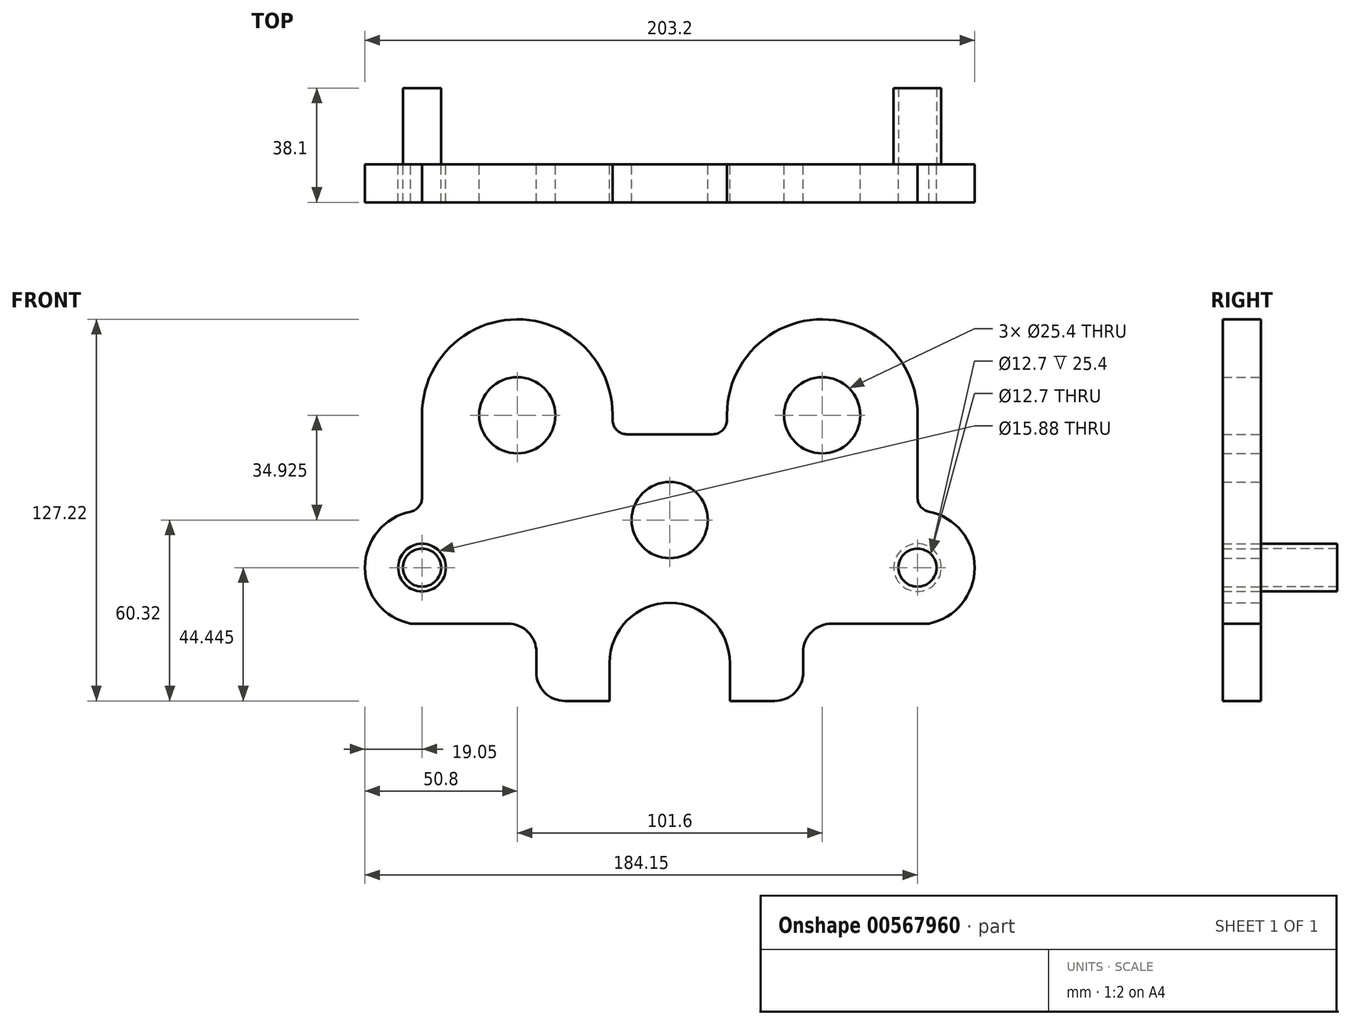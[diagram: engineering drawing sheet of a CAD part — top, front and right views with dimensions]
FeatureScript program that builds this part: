
annotation { "Feature Type Name" : "Feature", "Feature Type Description" : "" }
export const myFeature = defineFeature(function(context is Context, id is Id, definition is map)
    precondition{}
    {
        {
            var Q0;
            Q0=qCreatedBy(makeId("Front.planeOp"),FACE);
            var sketch = newSketch(context, id + "F0", { "sketchPlane" : qUnion([Q0])});
            skLineSegment(sketch, "E0", {"start": v(0, 79.1) * mm, "end": v(0, -74.39) * mm, "construction": true});
            skLineSegment(sketch, "E1", {"start": v(-86.36, 0) * mm, "end": v(95.43, 0) * mm, "construction": true});
            skLineSegment(sketch, "E2", {"start": v(50.8, 47.26) * mm, "end": v(50.8, 24.4) * mm, "construction": true});
            skLineSegment(sketch, "E3", {"start": v(82.55, -4.26) * mm, "end": v(82.55, -30.93) * mm, "construction": true});
            skLineSegment(sketch, "E4", {"start": v(-25.4, -47.62) * mm, "end": v(22.13, -47.62) * mm, "construction": true});
            skLineSegment(sketch, "E5", {"start": v(63.27, -15.88) * mm, "end": v(102.7, -15.88) * mm, "construction": true});
            skLineSegment(sketch, "E6", {"start": v(31.78, 34.93) * mm, "end": v(71.21, 34.93) * mm, "construction": true});
            skPoint(sketch, "E7", {"position": v(50.8, 34.93) * mm});
            skPoint(sketch, "E8", {"position": v(82.55, -15.88) * mm});
            skPoint(sketch, "E9", {"position": v(0, -47.62) * mm});
            skCircle(sketch, "E10", {"center": v(50.8, 34.93) * mm, "radius": 12.7 * mm});
            skCircle(sketch, "E11", {"center": v(82.55, -15.88) * mm, "radius": 6.35 * mm});
            skCircle(sketch, "E12", {"center": v(0, 0) * mm, "radius": 12.7 * mm});
            skLineSegment(sketch, "E13", {"start": v(-14.29, 28.57) * mm, "end": v(14.29, 28.57) * mm});
            skLineSegment(sketch, "E14", {"start": v(19.05, 35.15) * mm, "end": v(19.05, 33.34) * mm});
            skLineSegment(sketch, "E15", {"start": v(82.55, 34.93) * mm, "end": v(82.55, 7.46) * mm});
            skLineSegment(sketch, "E16", {"start": v(20.02, -60.32) * mm, "end": v(34.93, -60.32) * mm});
            skLineSegment(sketch, "E17", {"start": v(44.45, -50.8) * mm, "end": v(44.45, -44.07) * mm});
            skLineSegment(sketch, "E18", {"start": v(53.98, -34.54) * mm, "end": v(82.55, -34.54) * mm});
            skLineSegment(sketch, "E19", {"start": v(82.55, -34.54) * mm, "end": v(86.36, -34.54) * mm});
            skArc(sketch, "E20", {"start": v(19.05, 35.15) * mm, "mid": v(50.91, 66.9) * mm, "end": v(82.55, 34.93) * mm});
            skPoint(sketch, "E21.visualSharp", {"position": v(44.45, -34.54) * mm});
            skArc(sketch, "E21.filletArc", {"start": v(53.98, -34.54) * mm, "mid": v(47.24, -37.33) * mm, "end": v(44.45, -44.07) * mm});
            skPoint(sketch, "E22.visualSharp", {"position": v(44.45, -60.32) * mm});
            skArc(sketch, "E22.filletArc", {"start": v(34.93, -60.32) * mm, "mid": v(41.66, -57.54) * mm, "end": v(44.45, -50.8) * mm});
            skPoint(sketch, "E23.visualSharp", {"position": v(82.55, 3.18) * mm});
            skArc(sketch, "E23.filletArc", {"start": v(82.55, 7.46) * mm, "mid": v(83.62, 4.44) * mm, "end": v(86.36, 2.8) * mm});
            skArc(sketch, "E24", {"start": v(86.36, 2.8) * mm, "mid": v(101.6, -15.88) * mm, "end": v(86.36, -34.54) * mm});
            skLineSegment(sketch, "E25", {"start": v(20.02, -60.33) * mm, "end": v(20.02, -47.62) * mm});
            skLineSegment(sketch, "E26.MirrorCS", {"start": v(-20.02, -60.33) * mm, "end": v(-20.02, -47.62) * mm});
            skLineSegment(sketch, "E27.MirrorCS", {"start": v(-20.02, -60.32) * mm, "end": v(-34.93, -60.32) * mm});
            skArc(sketch, "E28.MirrorCS", {"start": v(-34.93, -60.32) * mm, "mid": v(-41.66, -57.54) * mm, "end": v(-44.45, -50.8) * mm});
            skLineSegment(sketch, "E29.MirrorCS", {"start": v(-44.45, -50.8) * mm, "end": v(-44.45, -44.07) * mm});
            skArc(sketch, "E30.MirrorCS", {"start": v(-53.98, -34.54) * mm, "mid": v(-47.24, -37.33) * mm, "end": v(-44.45, -44.07) * mm});
            skLineSegment(sketch, "E31.MirrorCS", {"start": v(-53.98, -34.54) * mm, "end": v(-82.55, -34.54) * mm});
            skLineSegment(sketch, "E32.MirrorCS", {"start": v(-82.55, -34.54) * mm, "end": v(-86.36, -34.54) * mm});
            skArc(sketch, "E33.MirrorCS", {"start": v(-86.36, 2.8) * mm, "mid": v(-101.6, -15.88) * mm, "end": v(-86.36, -34.54) * mm});
            skArc(sketch, "E34.MirrorCS", {"start": v(-82.55, 7.46) * mm, "mid": v(-83.62, 4.44) * mm, "end": v(-86.36, 2.8) * mm});
            skLineSegment(sketch, "E35.MirrorCS", {"start": v(-82.55, 34.93) * mm, "end": v(-82.55, 7.46) * mm});
            skArc(sketch, "E36.MirrorCS", {"start": v(-19.05, 35.15) * mm, "mid": v(-50.91, 66.9) * mm, "end": v(-82.55, 34.93) * mm});
            skLineSegment(sketch, "E37.MirrorCS", {"start": v(-19.05, 35.15) * mm, "end": v(-19.05, 33.34) * mm});
            skArc(sketch, "E38", {"start": v(-20.02, -47.62) * mm, "mid": v(0, -27.6) * mm, "end": v(20.02, -47.62) * mm});
            skCircle(sketch, "E39.MirrorC", {"center": v(-50.8, 34.93) * mm, "radius": 12.7 * mm});
            skCircle(sketch, "E40.MirrorC", {"center": v(-82.55, -15.88) * mm, "radius": 6.35 * mm});
            skPoint(sketch, "E41.visualSharp", {"position": v(-19.05, 28.57) * mm});
            skArc(sketch, "E41.filletArc", {"start": v(-19.05, 33.34) * mm, "mid": v(-17.66, 29.97) * mm, "end": v(-14.29, 28.57) * mm});
            skPoint(sketch, "E42.visualSharp", {"position": v(19.05, 28.58) * mm});
            skArc(sketch, "E42.filletArc", {"start": v(14.29, 28.57) * mm, "mid": v(17.66, 29.97) * mm, "end": v(19.05, 33.34) * mm});
            skCircle(sketch, "E43", {"center": v(82.55, -15.88) * mm, "radius": 7.94 * mm});
            skCircle(sketch, "E44.MirrorC", {"center": v(-82.55, -15.88) * mm, "radius": 7.94 * mm});
            skSolve(sketch);
        }
        {
            var Q0;
            Q0=makeQuery(id+"F0.imprint","IMPRINT",FACE,{"disambiguationData":[TD([[makeQuery(id+"F0.imprint","IMPRINT",EDGE,{"derivedFrom":sQuery(id+"F0.wireOp",EDGE,"E10")}),-1.0]])]});
            var Q1;
            Q1=makeQuery(id+"F0.imprint","IMPRINT",FACE,{"disambiguationData":[TD([[makeQuery(id+"F0.imprint","IMPRINT",EDGE,{"derivedFrom":sQuery(id+"F0.wireOp",EDGE,"E11")}),-1.0]])]});
            var Q2;
            Q2=makeQuery(id+"F0.imprint","IMPRINT",FACE,{"disambiguationData":[TD([[makeQuery(id+"F0.imprint","IMPRINT",EDGE,{"derivedFrom":sQuery(id+"F0.wireOp",EDGE,"E40.MirrorC")}),1.0]])]});
            extrude(context, id + "F1", {"entities" : qUnion([Q0, Q1, Q2]), "depth" : 12.7 * mm, "offsetDistance" : 25.4 * mm});
        }
        {
            var Q0;
            Q0=makeQuery(id+"F0.imprint","IMPRINT",FACE,{"disambiguationData":[TD([[makeQuery(id+"F0.imprint","IMPRINT",EDGE,{"derivedFrom":sQuery(id+"F0.wireOp",EDGE,"E40.MirrorC")}),1.0]])]});
            var Q1;
            Q1=makeQuery(id+"F0.imprint","IMPRINT",FACE,{"disambiguationData":[TD([[makeQuery(id+"F0.imprint","IMPRINT",EDGE,{"derivedFrom":sQuery(id+"F0.wireOp",EDGE,"E11")}),-1.0]])]});
            extrude(context, id + "F2", {"entities" : qUnion([Q0, Q1]), "oppositeDirection" : true, "depth" : 25.4 * mm, "offsetDistance" : 25.4 * mm});
        }
    });
